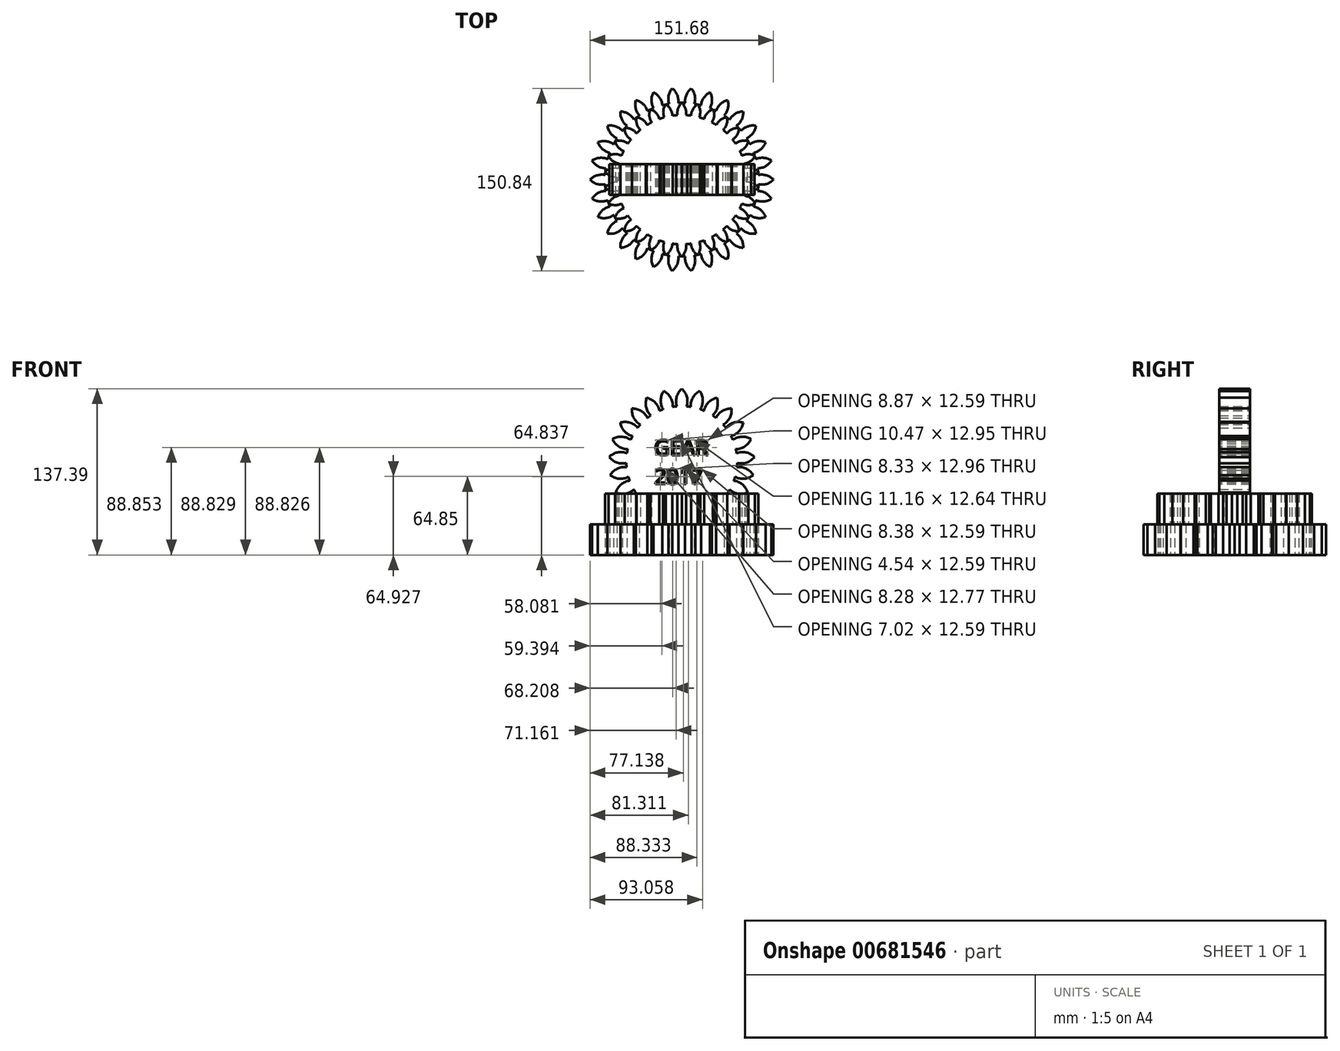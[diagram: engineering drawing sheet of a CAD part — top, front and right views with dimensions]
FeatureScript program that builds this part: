
annotation { "Feature Type Name" : "Feature", "Feature Type Description" : "" }
export const myFeature = defineFeature(function(context is Context, id is Id, definition is map)
    precondition{}
    {
        {
            var Q0;
            Q0=qCreatedBy(makeId("Top.planeOp"),FACE);
            var sketch = newSketch(context, id + "F0", { "sketchPlane" : qUnion([Q0])});
            skCircle(sketch, "E0", {"center": v(0, 0) * mm, "radius": 63.5 * mm});
            skArc(sketch, "E1", {"start": v(-63.38, 3.83) * mm, "mid": v(-70.11, 3.54) * mm, "end": v(-75.84, 0) * mm});
            skArc(sketch, "E2.MirrorCS", {"start": v(-63.38, -3.83) * mm, "mid": v(-70.11, -3.54) * mm, "end": v(-75.84, 0) * mm});
            skArc(sketch, "E3", {"start": v(-63.38, 3.83) * mm, "mid": v(-63.96, 0) * mm, "end": v(-63.38, -3.83) * mm});
            skArc(sketch, "E4.1.0", {"start": v(-62.8, -9.43) * mm, "mid": v(-69.31, -11.11) * mm, "end": v(-74.18, -15.77) * mm});
            skArc(sketch, "E4.1.2", {"start": v(-61.2, -16.92) * mm, "mid": v(-67.84, -18.04) * mm, "end": v(-74.18, -15.77) * mm});
            skArc(sketch, "E4.2.0", {"start": v(-59.46, -22.28) * mm, "mid": v(-65.49, -25.28) * mm, "end": v(-69.28, -30.85) * mm});
            skArc(sketch, "E4.2.2", {"start": v(-56.35, -29.28) * mm, "mid": v(-62.6, -31.75) * mm, "end": v(-69.28, -30.85) * mm});
            skArc(sketch, "E4.3.0", {"start": v(-53.53, -34.16) * mm, "mid": v(-58.8, -38.35) * mm, "end": v(-61.35, -44.58) * mm});
            skArc(sketch, "E4.3.2", {"start": v(-49.03, -40.36) * mm, "mid": v(-54.64, -44.07) * mm, "end": v(-61.35, -44.58) * mm});
            skArc(sketch, "E4.4.0", {"start": v(-45.26, -44.54) * mm, "mid": v(-49.54, -49.73) * mm, "end": v(-50.75, -56.36) * mm});
            skArc(sketch, "E4.4.2", {"start": v(-39.57, -49.67) * mm, "mid": v(-44.28, -54.47) * mm, "end": v(-50.75, -56.36) * mm});
            skArc(sketch, "E4.5.0", {"start": v(-35, -52.98) * mm, "mid": v(-38.12, -58.95) * mm, "end": v(-37.92, -65.68) * mm});
            skArc(sketch, "E4.5.2", {"start": v(-28.38, -56.8) * mm, "mid": v(-31.99, -62.49) * mm, "end": v(-37.92, -65.68) * mm});
            skArc(sketch, "E4.6.0", {"start": v(-23.23, -59.1) * mm, "mid": v(-25.03, -65.59) * mm, "end": v(-23.44, -72.13) * mm});
            skArc(sketch, "E4.6.2", {"start": v(-15.94, -61.47) * mm, "mid": v(-18.3, -67.77) * mm, "end": v(-23.44, -72.13) * mm});
            skArc(sketch, "E4.7.0", {"start": v(-10.43, -62.64) * mm, "mid": v(-10.85, -69.36) * mm, "end": v(-7.93, -75.42) * mm});
            skArc(sketch, "E4.7.2", {"start": v(-2.82, -63.44) * mm, "mid": v(-3.8, -70.1) * mm, "end": v(-7.93, -75.42) * mm});
            skArc(sketch, "E4.8.0", {"start": v(2.82, -63.44) * mm, "mid": v(3.8, -70.1) * mm, "end": v(7.93, -75.42) * mm});
            skArc(sketch, "E4.8.2", {"start": v(10.43, -62.64) * mm, "mid": v(10.85, -69.36) * mm, "end": v(7.93, -75.42) * mm});
            skArc(sketch, "E4.9.0", {"start": v(15.94, -61.47) * mm, "mid": v(18.3, -67.77) * mm, "end": v(23.44, -72.13) * mm});
            skArc(sketch, "E4.9.2", {"start": v(23.23, -59.1) * mm, "mid": v(25.03, -65.59) * mm, "end": v(23.44, -72.13) * mm});
            skArc(sketch, "E4.10.0", {"start": v(28.38, -56.8) * mm, "mid": v(31.99, -62.49) * mm, "end": v(37.92, -65.68) * mm});
            skArc(sketch, "E4.10.2", {"start": v(35, -52.98) * mm, "mid": v(38.12, -58.95) * mm, "end": v(37.92, -65.68) * mm});
            skArc(sketch, "E4.11.0", {"start": v(39.57, -49.67) * mm, "mid": v(44.28, -54.47) * mm, "end": v(50.75, -56.36) * mm});
            skArc(sketch, "E4.11.2", {"start": v(45.26, -44.54) * mm, "mid": v(49.54, -49.73) * mm, "end": v(50.75, -56.36) * mm});
            skArc(sketch, "E4.12.0", {"start": v(49.03, -40.36) * mm, "mid": v(54.64, -44.07) * mm, "end": v(61.35, -44.58) * mm});
            skArc(sketch, "E4.12.2", {"start": v(53.53, -34.16) * mm, "mid": v(58.8, -38.35) * mm, "end": v(61.35, -44.58) * mm});
            skArc(sketch, "E4.13.0", {"start": v(56.35, -29.28) * mm, "mid": v(62.6, -31.75) * mm, "end": v(69.28, -30.85) * mm});
            skArc(sketch, "E4.13.2", {"start": v(59.46, -22.28) * mm, "mid": v(65.49, -25.28) * mm, "end": v(69.28, -30.85) * mm});
            skArc(sketch, "E4.14.0", {"start": v(61.2, -16.92) * mm, "mid": v(67.84, -18.04) * mm, "end": v(74.18, -15.77) * mm});
            skArc(sketch, "E4.14.2", {"start": v(62.8, -9.43) * mm, "mid": v(69.31, -11.11) * mm, "end": v(74.18, -15.77) * mm});
            skArc(sketch, "E5.3.15.0", {"start": v(63.38, -3.83) * mm, "mid": v(70.11, -3.54) * mm, "end": v(75.84, 0) * mm});
            skArc(sketch, "E5.6.15.0", {"start": v(63.38, 3.83) * mm, "mid": v(70.11, 3.54) * mm, "end": v(75.84, 0) * mm});
            skArc(sketch, "E5.3.16.0", {"start": v(62.8, 9.43) * mm, "mid": v(69.31, 11.11) * mm, "end": v(74.18, 15.77) * mm});
            skArc(sketch, "E5.6.16.0", {"start": v(61.2, 16.92) * mm, "mid": v(67.84, 18.04) * mm, "end": v(74.18, 15.77) * mm});
            skArc(sketch, "E5.3.17.0", {"start": v(59.46, 22.28) * mm, "mid": v(65.49, 25.28) * mm, "end": v(69.28, 30.85) * mm});
            skArc(sketch, "E5.6.17.0", {"start": v(56.35, 29.28) * mm, "mid": v(62.6, 31.75) * mm, "end": v(69.28, 30.85) * mm});
            skArc(sketch, "E5.3.18.0", {"start": v(53.53, 34.16) * mm, "mid": v(58.8, 38.35) * mm, "end": v(61.35, 44.58) * mm});
            skArc(sketch, "E5.6.18.0", {"start": v(49.03, 40.36) * mm, "mid": v(54.64, 44.07) * mm, "end": v(61.35, 44.58) * mm});
            skArc(sketch, "E5.3.19.0", {"start": v(45.26, 44.54) * mm, "mid": v(49.54, 49.73) * mm, "end": v(50.75, 56.36) * mm});
            skArc(sketch, "E5.6.19.0", {"start": v(39.57, 49.67) * mm, "mid": v(44.28, 54.47) * mm, "end": v(50.75, 56.36) * mm});
            skArc(sketch, "E5.3.20.0", {"start": v(35, 52.98) * mm, "mid": v(38.12, 58.95) * mm, "end": v(37.92, 65.68) * mm});
            skArc(sketch, "E5.6.20.0", {"start": v(28.38, 56.8) * mm, "mid": v(31.99, 62.49) * mm, "end": v(37.92, 65.68) * mm});
            skArc(sketch, "E5.3.21.0", {"start": v(23.23, 59.1) * mm, "mid": v(25.03, 65.59) * mm, "end": v(23.44, 72.13) * mm});
            skArc(sketch, "E5.6.21.0", {"start": v(15.94, 61.47) * mm, "mid": v(18.3, 67.77) * mm, "end": v(23.44, 72.13) * mm});
            skArc(sketch, "E5.3.22.0", {"start": v(10.43, 62.64) * mm, "mid": v(10.85, 69.36) * mm, "end": v(7.93, 75.42) * mm});
            skArc(sketch, "E5.6.22.0", {"start": v(2.82, 63.44) * mm, "mid": v(3.8, 70.1) * mm, "end": v(7.93, 75.42) * mm});
            skArc(sketch, "E5.3.23.0", {"start": v(-2.82, 63.44) * mm, "mid": v(-3.8, 70.1) * mm, "end": v(-7.93, 75.42) * mm});
            skArc(sketch, "E5.6.23.0", {"start": v(-10.43, 62.64) * mm, "mid": v(-10.85, 69.36) * mm, "end": v(-7.93, 75.42) * mm});
            skArc(sketch, "E5.3.24.0", {"start": v(-15.94, 61.47) * mm, "mid": v(-18.3, 67.77) * mm, "end": v(-23.44, 72.13) * mm});
            skArc(sketch, "E5.6.24.0", {"start": v(-23.23, 59.1) * mm, "mid": v(-25.03, 65.59) * mm, "end": v(-23.44, 72.13) * mm});
            skArc(sketch, "E5.3.25.0", {"start": v(-28.38, 56.8) * mm, "mid": v(-31.99, 62.49) * mm, "end": v(-37.92, 65.68) * mm});
            skArc(sketch, "E5.6.25.0", {"start": v(-35, 52.98) * mm, "mid": v(-38.12, 58.95) * mm, "end": v(-37.92, 65.68) * mm});
            skArc(sketch, "E5.3.26.0", {"start": v(-39.57, 49.67) * mm, "mid": v(-44.28, 54.47) * mm, "end": v(-50.75, 56.36) * mm});
            skArc(sketch, "E5.6.26.0", {"start": v(-45.26, 44.54) * mm, "mid": v(-49.54, 49.73) * mm, "end": v(-50.75, 56.36) * mm});
            skArc(sketch, "E5.3.27.0", {"start": v(-49.03, 40.36) * mm, "mid": v(-54.64, 44.07) * mm, "end": v(-61.35, 44.58) * mm});
            skArc(sketch, "E5.6.27.0", {"start": v(-53.53, 34.16) * mm, "mid": v(-58.8, 38.35) * mm, "end": v(-61.35, 44.58) * mm});
            skArc(sketch, "E5.3.28.0", {"start": v(-56.35, 29.28) * mm, "mid": v(-62.6, 31.75) * mm, "end": v(-69.28, 30.85) * mm});
            skArc(sketch, "E5.6.28.0", {"start": v(-59.46, 22.28) * mm, "mid": v(-65.49, 25.28) * mm, "end": v(-69.28, 30.85) * mm});
            skArc(sketch, "E5.3.29.0", {"start": v(-61.2, 16.92) * mm, "mid": v(-67.84, 18.04) * mm, "end": v(-74.18, 15.77) * mm});
            skArc(sketch, "E5.6.29.0", {"start": v(-62.8, 9.43) * mm, "mid": v(-69.31, 11.11) * mm, "end": v(-74.18, 15.77) * mm});
            skSolve(sketch);
        }
        {
            var Q0;
            Q0 = qSketchRegion(id + "F0", true);
            extrude(context, id + "F1", {"entities" : qUnion([Q0]), "depth" : 25.4 * mm, "offsetDistance" : 25.4 * mm});
        }
        {
            var Q0;
            Q0=makeQuery(id+"F1.opExtrude","CAP_FACE",FACE,{"disambiguationData":[OSD([sQuery(id+"F0.wireOp",EDGE,"E1"),sQuery(id+"F0.wireOp",EDGE,"E2.MirrorCS"),sQuery(id+"F0.wireOp",EDGE,"E4.1.0"),sQuery(id+"F0.wireOp",EDGE,"E4.1.2"),sQuery(id+"F0.wireOp",EDGE,"E4.2.0"),sQuery(id+"F0.wireOp",EDGE,"E4.2.2"),sQuery(id+"F0.wireOp",EDGE,"E4.3.0"),sQuery(id+"F0.wireOp",EDGE,"E4.3.2"),sQuery(id+"F0.wireOp",EDGE,"E4.4.0"),sQuery(id+"F0.wireOp",EDGE,"E4.4.2"),sQuery(id+"F0.wireOp",EDGE,"E4.5.0"),sQuery(id+"F0.wireOp",EDGE,"E4.5.2"),sQuery(id+"F0.wireOp",EDGE,"E4.6.0"),sQuery(id+"F0.wireOp",EDGE,"E4.6.2"),sQuery(id+"F0.wireOp",EDGE,"E4.7.0"),sQuery(id+"F0.wireOp",EDGE,"E4.7.2"),sQuery(id+"F0.wireOp",EDGE,"E4.8.0"),sQuery(id+"F0.wireOp",EDGE,"E4.8.2"),sQuery(id+"F0.wireOp",EDGE,"E4.9.0"),sQuery(id+"F0.wireOp",EDGE,"E4.9.2"),sQuery(id+"F0.wireOp",EDGE,"E4.10.0"),sQuery(id+"F0.wireOp",EDGE,"E4.10.2"),sQuery(id+"F0.wireOp",EDGE,"E4.11.0"),sQuery(id+"F0.wireOp",EDGE,"E4.11.2"),sQuery(id+"F0.wireOp",EDGE,"E4.12.0"),sQuery(id+"F0.wireOp",EDGE,"E4.12.2"),sQuery(id+"F0.wireOp",EDGE,"E4.13.0"),sQuery(id+"F0.wireOp",EDGE,"E4.13.2"),sQuery(id+"F0.wireOp",EDGE,"E4.14.0"),sQuery(id+"F0.wireOp",EDGE,"E4.14.2"),sQuery(id+"F0.wireOp",EDGE,"E5.3.15.0"),sQuery(id+"F0.wireOp",EDGE,"E5.6.15.0"),sQuery(id+"F0.wireOp",EDGE,"E5.3.16.0"),sQuery(id+"F0.wireOp",EDGE,"E5.6.16.0"),sQuery(id+"F0.wireOp",EDGE,"E5.3.17.0"),sQuery(id+"F0.wireOp",EDGE,"E5.6.17.0"),sQuery(id+"F0.wireOp",EDGE,"E5.3.18.0"),sQuery(id+"F0.wireOp",EDGE,"E5.6.18.0"),sQuery(id+"F0.wireOp",EDGE,"E5.3.19.0"),sQuery(id+"F0.wireOp",EDGE,"E5.6.19.0"),sQuery(id+"F0.wireOp",EDGE,"E5.3.20.0"),sQuery(id+"F0.wireOp",EDGE,"E5.6.20.0"),sQuery(id+"F0.wireOp",EDGE,"E5.3.21.0"),sQuery(id+"F0.wireOp",EDGE,"E5.6.21.0"),sQuery(id+"F0.wireOp",EDGE,"E5.3.22.0"),sQuery(id+"F0.wireOp",EDGE,"E5.6.22.0"),sQuery(id+"F0.wireOp",EDGE,"E5.3.23.0"),sQuery(id+"F0.wireOp",EDGE,"E5.6.23.0"),sQuery(id+"F0.wireOp",EDGE,"E5.3.24.0"),sQuery(id+"F0.wireOp",EDGE,"E5.6.24.0"),sQuery(id+"F0.wireOp",EDGE,"E5.3.25.0"),sQuery(id+"F0.wireOp",EDGE,"E5.6.25.0"),sQuery(id+"F0.wireOp",EDGE,"E5.3.26.0"),sQuery(id+"F0.wireOp",EDGE,"E5.6.26.0"),sQuery(id+"F0.wireOp",EDGE,"E5.3.27.0"),sQuery(id+"F0.wireOp",EDGE,"E5.6.27.0"),sQuery(id+"F0.wireOp",EDGE,"E5.3.28.0"),sQuery(id+"F0.wireOp",EDGE,"E5.6.28.0"),sQuery(id+"F0.wireOp",EDGE,"E5.3.29.0"),sQuery(id+"F0.wireOp",EDGE,"E0"),sQuery(id+"F0.wireOp",EDGE,"E5.6.29.0")])],"isStart":false});
            var sketch = newSketch(context, id + "F2", { "sketchPlane" : qUnion([Q0])});
            skCircle(sketch, "E6", {"center": v(0, 0) * mm, "radius": 53.5 * mm});
            skArc(sketch, "E7", {"start": v(-52.74, 9) * mm, "mid": v(-58.36, 9.16) * mm, "end": v(-63.38, 6.64) * mm});
            skPoint(sketch, "E7.endSnap0", {"position": v(-63.15, 6.64) * mm});
            skLineSegment(sketch, "E8", {"start": v(0, 0) * mm, "end": v(-63.15, 6.64) * mm});
            skArc(sketch, "E9.MirrorCS", {"start": v(-53.46, 2.16) * mm, "mid": v(-58.99, 3.17) * mm, "end": v(-63.38, 6.69) * mm});
            skArc(sketch, "E10", {"start": v(-53.46, 2.16) * mm, "mid": v(-53.09, 5.58) * mm, "end": v(-52.74, 9) * mm});
            skArc(sketch, "E11.1.0", {"start": v(-53.46, -2.16) * mm, "mid": v(-58.99, -3.17) * mm, "end": v(-63.38, -6.69) * mm});
            skArc(sketch, "E11.1.1", {"start": v(-52.74, -9) * mm, "mid": v(-58.36, -9.16) * mm, "end": v(-63.38, -6.64) * mm});
            skArc(sketch, "E11.2.0", {"start": v(-51.84, -13.23) * mm, "mid": v(-57.04, -15.37) * mm, "end": v(-60.6, -19.72) * mm});
            skArc(sketch, "E11.2.1", {"start": v(-49.71, -19.77) * mm, "mid": v(-55.18, -21.1) * mm, "end": v(-60.62, -19.67) * mm});
            skArc(sketch, "E11.3.0", {"start": v(-47.96, -23.71) * mm, "mid": v(-52.6, -26.9) * mm, "end": v(-55.18, -31.89) * mm});
            skArc(sketch, "E11.3.1", {"start": v(-44.52, -29.68) * mm, "mid": v(-49.59, -32.1) * mm, "end": v(-55.2, -31.84) * mm});
            skArc(sketch, "E11.4.0", {"start": v(-41.98, -33.17) * mm, "mid": v(-45.86, -37.24) * mm, "end": v(-47.35, -42.66) * mm});
            skArc(sketch, "E11.4.1", {"start": v(-37.37, -38.28) * mm, "mid": v(-41.83, -41.71) * mm, "end": v(-47.38, -42.63) * mm});
            skArc(sketch, "E11.5.0", {"start": v(-34.17, -41.17) * mm, "mid": v(-37.11, -45.96) * mm, "end": v(-37.44, -51.57) * mm});
            skArc(sketch, "E11.5.1", {"start": v(-28.6, -45.22) * mm, "mid": v(-32.24, -49.5) * mm, "end": v(-37.48, -51.55) * mm});
            skArc(sketch, "E11.6.0", {"start": v(-24.86, -47.37) * mm, "mid": v(-26.75, -52.67) * mm, "end": v(-25.9, -58.23) * mm});
            skArc(sketch, "E11.6.1", {"start": v(-18.57, -50.17) * mm, "mid": v(-21.25, -55.12) * mm, "end": v(-25.94, -58.21) * mm});
            skArc(sketch, "E11.7.0", {"start": v(-14.47, -51.5) * mm, "mid": v(-15.21, -57.08) * mm, "end": v(-13.23, -62.34) * mm});
            skArc(sketch, "E11.7.1", {"start": v(-7.73, -52.94) * mm, "mid": v(-9.32, -58.33) * mm, "end": v(-13.27, -62.33) * mm});
            skArc(sketch, "E11.8.0", {"start": v(-3.44, -53.4) * mm, "mid": v(-3.01, -59) * mm, "end": v(0.02, -63.73) * mm});
            skArc(sketch, "E11.8.1", {"start": v(3.44, -53.4) * mm, "mid": v(3.01, -59) * mm, "end": v(-0.02, -63.73) * mm});
            skArc(sketch, "E11.9.0", {"start": v(7.73, -52.94) * mm, "mid": v(9.32, -58.33) * mm, "end": v(13.27, -62.33) * mm});
            skArc(sketch, "E11.9.1", {"start": v(14.47, -51.5) * mm, "mid": v(15.21, -57.08) * mm, "end": v(13.23, -62.34) * mm});
            skArc(sketch, "E11.10.0", {"start": v(18.57, -50.17) * mm, "mid": v(21.25, -55.12) * mm, "end": v(25.94, -58.21) * mm});
            skArc(sketch, "E11.10.1", {"start": v(24.86, -47.37) * mm, "mid": v(26.75, -52.67) * mm, "end": v(25.9, -58.23) * mm});
            skArc(sketch, "E11.11.0", {"start": v(28.6, -45.22) * mm, "mid": v(32.24, -49.5) * mm, "end": v(37.48, -51.55) * mm});
            skArc(sketch, "E11.11.1", {"start": v(34.17, -41.17) * mm, "mid": v(37.11, -45.96) * mm, "end": v(37.44, -51.57) * mm});
            skArc(sketch, "E11.12.0", {"start": v(37.37, -38.28) * mm, "mid": v(41.83, -41.71) * mm, "end": v(47.38, -42.63) * mm});
            skArc(sketch, "E11.12.1", {"start": v(41.98, -33.17) * mm, "mid": v(45.86, -37.24) * mm, "end": v(47.35, -42.66) * mm});
            skArc(sketch, "E11.13.0", {"start": v(44.52, -29.68) * mm, "mid": v(49.59, -32.1) * mm, "end": v(55.2, -31.84) * mm});
            skArc(sketch, "E11.13.1", {"start": v(47.96, -23.71) * mm, "mid": v(52.6, -26.9) * mm, "end": v(55.18, -31.89) * mm});
            skArc(sketch, "E11.14.0", {"start": v(49.71, -19.77) * mm, "mid": v(55.18, -21.1) * mm, "end": v(60.62, -19.67) * mm});
            skArc(sketch, "E11.14.1", {"start": v(51.84, -13.23) * mm, "mid": v(57.04, -15.37) * mm, "end": v(60.6, -19.72) * mm});
            skArc(sketch, "E11.15.0", {"start": v(52.74, -9) * mm, "mid": v(58.36, -9.16) * mm, "end": v(63.38, -6.64) * mm});
            skArc(sketch, "E11.15.1", {"start": v(53.46, -2.16) * mm, "mid": v(58.99, -3.17) * mm, "end": v(63.38, -6.69) * mm});
            skArc(sketch, "E11.16.0", {"start": v(53.46, 2.16) * mm, "mid": v(58.99, 3.17) * mm, "end": v(63.38, 6.69) * mm});
            skArc(sketch, "E11.16.1", {"start": v(52.74, 9) * mm, "mid": v(58.36, 9.16) * mm, "end": v(63.38, 6.64) * mm});
            skArc(sketch, "E11.17.0", {"start": v(51.84, 13.23) * mm, "mid": v(57.04, 15.37) * mm, "end": v(60.6, 19.72) * mm});
            skArc(sketch, "E11.17.1", {"start": v(49.71, 19.77) * mm, "mid": v(55.18, 21.1) * mm, "end": v(60.62, 19.67) * mm});
            skArc(sketch, "E11.18.0", {"start": v(47.96, 23.71) * mm, "mid": v(52.6, 26.9) * mm, "end": v(55.18, 31.89) * mm});
            skArc(sketch, "E11.18.1", {"start": v(44.52, 29.68) * mm, "mid": v(49.59, 32.1) * mm, "end": v(55.2, 31.84) * mm});
            skArc(sketch, "E11.19.0", {"start": v(41.98, 33.17) * mm, "mid": v(45.86, 37.24) * mm, "end": v(47.35, 42.66) * mm});
            skArc(sketch, "E11.19.1", {"start": v(37.37, 38.28) * mm, "mid": v(41.83, 41.71) * mm, "end": v(47.38, 42.63) * mm});
            skArc(sketch, "E11.20.0", {"start": v(34.17, 41.17) * mm, "mid": v(37.11, 45.96) * mm, "end": v(37.44, 51.57) * mm});
            skArc(sketch, "E11.20.1", {"start": v(28.6, 45.22) * mm, "mid": v(32.24, 49.5) * mm, "end": v(37.48, 51.55) * mm});
            skArc(sketch, "E11.21.0", {"start": v(24.86, 47.37) * mm, "mid": v(26.75, 52.67) * mm, "end": v(25.9, 58.23) * mm});
            skArc(sketch, "E11.21.1", {"start": v(18.57, 50.17) * mm, "mid": v(21.25, 55.12) * mm, "end": v(25.94, 58.21) * mm});
            skArc(sketch, "E11.22.0", {"start": v(14.47, 51.5) * mm, "mid": v(15.21, 57.08) * mm, "end": v(13.23, 62.34) * mm});
            skArc(sketch, "E11.22.1", {"start": v(7.73, 52.94) * mm, "mid": v(9.32, 58.33) * mm, "end": v(13.27, 62.33) * mm});
            skArc(sketch, "E11.23.0", {"start": v(3.44, 53.4) * mm, "mid": v(3.01, 59) * mm, "end": v(-0.02, 63.73) * mm});
            skArc(sketch, "E11.23.1", {"start": v(-3.44, 53.4) * mm, "mid": v(-3.01, 59) * mm, "end": v(0.02, 63.73) * mm});
            skArc(sketch, "E11.24.0", {"start": v(-7.73, 52.94) * mm, "mid": v(-9.32, 58.33) * mm, "end": v(-13.27, 62.33) * mm});
            skArc(sketch, "E11.24.1", {"start": v(-14.47, 51.5) * mm, "mid": v(-15.21, 57.08) * mm, "end": v(-13.23, 62.34) * mm});
            skArc(sketch, "E11.25.0", {"start": v(-18.57, 50.17) * mm, "mid": v(-21.25, 55.12) * mm, "end": v(-25.94, 58.21) * mm});
            skArc(sketch, "E11.25.1", {"start": v(-24.86, 47.37) * mm, "mid": v(-26.75, 52.67) * mm, "end": v(-25.9, 58.23) * mm});
            skArc(sketch, "E11.26.0", {"start": v(-28.6, 45.22) * mm, "mid": v(-32.24, 49.5) * mm, "end": v(-37.48, 51.55) * mm});
            skArc(sketch, "E11.26.1", {"start": v(-34.17, 41.17) * mm, "mid": v(-37.11, 45.96) * mm, "end": v(-37.44, 51.57) * mm});
            skArc(sketch, "E11.27.0", {"start": v(-37.37, 38.28) * mm, "mid": v(-41.83, 41.71) * mm, "end": v(-47.38, 42.63) * mm});
            skArc(sketch, "E11.27.1", {"start": v(-41.98, 33.17) * mm, "mid": v(-45.86, 37.24) * mm, "end": v(-47.35, 42.66) * mm});
            skArc(sketch, "E11.28.0", {"start": v(-44.52, 29.68) * mm, "mid": v(-49.59, 32.1) * mm, "end": v(-55.2, 31.84) * mm});
            skArc(sketch, "E11.28.1", {"start": v(-47.96, 23.71) * mm, "mid": v(-52.6, 26.9) * mm, "end": v(-55.18, 31.89) * mm});
            skArc(sketch, "E11.29.0", {"start": v(-49.71, 19.77) * mm, "mid": v(-55.18, 21.1) * mm, "end": v(-60.62, 19.67) * mm});
            skArc(sketch, "E11.29.1", {"start": v(-51.84, 13.23) * mm, "mid": v(-57.04, 15.37) * mm, "end": v(-60.6, 19.72) * mm});
            skSolve(sketch);
        }
        {
            var Q0;
            Q0 = qSketchRegion(id + "F2", true);
            extrude(context, id + "F3", {"entities" : qUnion([Q0]), "operationType" : NewBodyOperationType.ADD, "depth" : 25.4 * mm, "offsetDistance" : 25.4 * mm});
        }
        {
            var Q0;
            Q0=qCreatedBy(makeId("Front.planeOp"),FACE);
            var sketch = newSketch(context, id + "F4", { "sketchPlane" : qUnion([Q0])});
            skCircle(sketch, "E12", {"center": v(0, 77.24) * mm, "radius": 45.85 * mm});
            skArc(sketch, "E13", {"start": v(4.07, 122.9) * mm, "mid": v(4.18, 130.75) * mm, "end": v(0, 137.39) * mm});
            skArc(sketch, "E14.MirrorCS", {"start": v(-4.07, 122.9) * mm, "mid": v(-4.18, 130.75) * mm, "end": v(0, 137.39) * mm});
            skArc(sketch, "E15", {"start": v(-4.07, 122.9) * mm, "mid": v(0, 122.88) * mm, "end": v(4.07, 122.9) * mm});
            skPoint(sketch, "E16.center", {"position": v(0, 0) * mm});
            skArc(sketch, "E17.1.0", {"start": v(-15.3, 120.46) * mm, "mid": v(-17.36, 128.03) * mm, "end": v(-14.96, 135.5) * mm});
            skArc(sketch, "E17.1.1", {"start": v(-7.42, 122.48) * mm, "mid": v(-9.26, 130.1) * mm, "end": v(-14.96, 135.5) * mm});
            skArc(sketch, "E17.2.0", {"start": v(-25.56, 115.3) * mm, "mid": v(-29.44, 122.11) * mm, "end": v(-28.98, 129.95) * mm});
            skArc(sketch, "E17.2.1", {"start": v(-18.44, 119.21) * mm, "mid": v(-22.12, 126.14) * mm, "end": v(-28.98, 129.95) * mm});
            skArc(sketch, "E17.3.0", {"start": v(-34.23, 107.74) * mm, "mid": v(-39.68, 113.38) * mm, "end": v(-41.18, 121.08) * mm});
            skArc(sketch, "E17.3.1", {"start": v(-28.3, 113.3) * mm, "mid": v(-33.58, 119.1) * mm, "end": v(-41.18, 121.08) * mm});
            skArc(sketch, "E17.4.0", {"start": v(-40.74, 98.27) * mm, "mid": v(-47.42, 102.38) * mm, "end": v(-50.79, 109.47) * mm});
            skArc(sketch, "E17.4.1", {"start": v(-36.38, 105.14) * mm, "mid": v(-42.94, 109.44) * mm, "end": v(-50.79, 109.47) * mm});
            skArc(sketch, "E17.5.0", {"start": v(-44.69, 87.48) * mm, "mid": v(-52.18, 89.8) * mm, "end": v(-57.2, 95.82) * mm});
            skArc(sketch, "E17.5.1", {"start": v(-42.17, 95.22) * mm, "mid": v(-49.6, 97.75) * mm, "end": v(-57.2, 95.82) * mm});
            skArc(sketch, "E17.6.0", {"start": v(-45.83, 76.04) * mm, "mid": v(-53.67, 76.42) * mm, "end": v(-60.03, 81.01) * mm});
            skArc(sketch, "E17.6.1", {"start": v(-45.32, 84.16) * mm, "mid": v(-53.14, 84.77) * mm, "end": v(-60.03, 81.01) * mm});
            skArc(sketch, "E17.7.0", {"start": v(-44.1, 64.68) * mm, "mid": v(-51.78, 63.1) * mm, "end": v(-59.08, 65.97) * mm});
            skArc(sketch, "E17.7.1", {"start": v(-45.62, 72.67) * mm, "mid": v(-53.35, 71.32) * mm, "end": v(-59.08, 65.97) * mm});
            skArc(sketch, "E17.8.0", {"start": v(-39.59, 54.11) * mm, "mid": v(-46.64, 50.67) * mm, "end": v(-54.42, 51.63) * mm});
            skArc(sketch, "E17.8.1", {"start": v(-43.05, 61.47) * mm, "mid": v(-50.2, 58.23) * mm, "end": v(-54.42, 51.63) * mm});
            skArc(sketch, "E17.9.0", {"start": v(-32.6, 45) * mm, "mid": v(-38.57, 39.9) * mm, "end": v(-46.35, 38.9) * mm});
            skArc(sketch, "E17.9.1", {"start": v(-37.78, 51.26) * mm, "mid": v(-43.9, 46.35) * mm, "end": v(-46.35, 38.9) * mm});
            skArc(sketch, "E17.10.0", {"start": v(-23.55, 37.9) * mm, "mid": v(-28.07, 31.49) * mm, "end": v(-35.35, 28.57) * mm});
            skArc(sketch, "E17.10.1", {"start": v(-30.13, 42.68) * mm, "mid": v(-34.84, 36.4) * mm, "end": v(-35.35, 28.57) * mm});
            skArc(sketch, "E17.11.0", {"start": v(-13.03, 33.28) * mm, "mid": v(-15.81, 25.94) * mm, "end": v(-22.14, 21.31) * mm});
            skArc(sketch, "E17.11.1", {"start": v(-20.6, 36.27) * mm, "mid": v(-23.59, 29.02) * mm, "end": v(-22.14, 21.31) * mm});
            skArc(sketch, "E17.12.0", {"start": v(-1.69, 31.42) * mm, "mid": v(-2.56, 23.62) * mm, "end": v(-7.54, 17.56) * mm});
            skArc(sketch, "E17.12.1", {"start": v(-9.76, 32.44) * mm, "mid": v(-10.85, 24.67) * mm, "end": v(-7.54, 17.56) * mm});
            skArc(sketch, "E17.13.0", {"start": v(9.76, 32.44) * mm, "mid": v(10.85, 24.67) * mm, "end": v(7.54, 17.56) * mm});
            skArc(sketch, "E17.13.1", {"start": v(1.69, 31.42) * mm, "mid": v(2.56, 23.62) * mm, "end": v(7.54, 17.56) * mm});
            skArc(sketch, "E17.14.0", {"start": v(20.6, 36.27) * mm, "mid": v(23.59, 29.02) * mm, "end": v(22.14, 21.31) * mm});
            skArc(sketch, "E17.14.1", {"start": v(13.03, 33.28) * mm, "mid": v(15.81, 25.94) * mm, "end": v(22.14, 21.31) * mm});
            skArc(sketch, "E17.15.0", {"start": v(30.13, 42.68) * mm, "mid": v(34.84, 36.4) * mm, "end": v(35.35, 28.57) * mm});
            skArc(sketch, "E17.15.1", {"start": v(23.55, 37.9) * mm, "mid": v(28.07, 31.49) * mm, "end": v(35.35, 28.57) * mm});
            skArc(sketch, "E17.16.0", {"start": v(37.78, 51.26) * mm, "mid": v(43.9, 46.35) * mm, "end": v(46.35, 38.9) * mm});
            skArc(sketch, "E17.16.1", {"start": v(32.6, 45) * mm, "mid": v(38.57, 39.9) * mm, "end": v(46.35, 38.9) * mm});
            skArc(sketch, "E17.17.0", {"start": v(43.05, 61.47) * mm, "mid": v(50.2, 58.23) * mm, "end": v(54.42, 51.63) * mm});
            skArc(sketch, "E17.17.1", {"start": v(39.59, 54.11) * mm, "mid": v(46.64, 50.67) * mm, "end": v(54.42, 51.63) * mm});
            skArc(sketch, "E17.18.0", {"start": v(45.62, 72.67) * mm, "mid": v(53.35, 71.32) * mm, "end": v(59.08, 65.97) * mm});
            skArc(sketch, "E17.18.1", {"start": v(44.1, 64.68) * mm, "mid": v(51.78, 63.1) * mm, "end": v(59.08, 65.97) * mm});
            skArc(sketch, "E17.19.0", {"start": v(45.32, 84.16) * mm, "mid": v(53.14, 84.77) * mm, "end": v(60.03, 81.01) * mm});
            skArc(sketch, "E17.19.1", {"start": v(45.83, 76.04) * mm, "mid": v(53.67, 76.42) * mm, "end": v(60.03, 81.01) * mm});
            skArc(sketch, "E17.20.0", {"start": v(42.17, 95.22) * mm, "mid": v(49.6, 97.75) * mm, "end": v(57.2, 95.82) * mm});
            skArc(sketch, "E17.20.1", {"start": v(44.69, 87.48) * mm, "mid": v(52.18, 89.8) * mm, "end": v(57.2, 95.82) * mm});
            skArc(sketch, "E17.21.0", {"start": v(36.38, 105.14) * mm, "mid": v(42.94, 109.44) * mm, "end": v(50.79, 109.47) * mm});
            skArc(sketch, "E17.21.1", {"start": v(40.74, 98.27) * mm, "mid": v(47.42, 102.38) * mm, "end": v(50.79, 109.47) * mm});
            skArc(sketch, "E17.22.0", {"start": v(28.3, 113.3) * mm, "mid": v(33.58, 119.1) * mm, "end": v(41.18, 121.08) * mm});
            skArc(sketch, "E17.22.1", {"start": v(34.23, 107.74) * mm, "mid": v(39.68, 113.38) * mm, "end": v(41.18, 121.08) * mm});
            skArc(sketch, "E17.23.0", {"start": v(18.44, 119.21) * mm, "mid": v(22.12, 126.14) * mm, "end": v(28.98, 129.95) * mm});
            skArc(sketch, "E17.23.1", {"start": v(25.56, 115.3) * mm, "mid": v(29.44, 122.11) * mm, "end": v(28.98, 129.95) * mm});
            skArc(sketch, "E17.24.0", {"start": v(7.42, 122.48) * mm, "mid": v(9.26, 130.1) * mm, "end": v(14.96, 135.5) * mm});
            skArc(sketch, "E17.24.1", {"start": v(15.3, 120.46) * mm, "mid": v(17.36, 128.03) * mm, "end": v(14.96, 135.5) * mm});
            skSolve(sketch);
        }
        {
            var Q0;
            Q0 = qSketchRegion(id + "F4", true);
            extrude(context, id + "F5", {"entities" : qUnion([Q0]), "operationType" : NewBodyOperationType.ADD, "endBound" : BoundingType.SYMMETRIC, "depth" : 25.4 * mm, "offsetDistance" : 25.4 * mm});
        }
        {
            var Q0;
            Q0=makeQuery(id+"F5.opExtrude","CAP_FACE",FACE,{"disambiguationData":[OSD([sQuery(id+"F4.wireOp",EDGE,"E12"),sQuery(id+"F4.wireOp",EDGE,"E13"),sQuery(id+"F4.wireOp",EDGE,"E14.MirrorCS"),sQuery(id+"F4.wireOp",EDGE,"E17.1.0"),sQuery(id+"F4.wireOp",EDGE,"E17.1.1"),sQuery(id+"F4.wireOp",EDGE,"E17.2.0"),sQuery(id+"F4.wireOp",EDGE,"E17.2.1"),sQuery(id+"F4.wireOp",EDGE,"E17.3.0"),sQuery(id+"F4.wireOp",EDGE,"E17.3.1"),sQuery(id+"F4.wireOp",EDGE,"E17.4.0"),sQuery(id+"F4.wireOp",EDGE,"E17.4.1"),sQuery(id+"F4.wireOp",EDGE,"E17.5.0"),sQuery(id+"F4.wireOp",EDGE,"E17.5.1"),sQuery(id+"F4.wireOp",EDGE,"E17.6.0"),sQuery(id+"F4.wireOp",EDGE,"E17.6.1"),sQuery(id+"F4.wireOp",EDGE,"E17.7.0"),sQuery(id+"F4.wireOp",EDGE,"E17.7.1"),sQuery(id+"F4.wireOp",EDGE,"E17.8.0"),sQuery(id+"F4.wireOp",EDGE,"E17.8.1"),sQuery(id+"F4.wireOp",EDGE,"E17.9.0"),sQuery(id+"F4.wireOp",EDGE,"E17.9.1"),sQuery(id+"F4.wireOp",EDGE,"E17.10.0"),sQuery(id+"F4.wireOp",EDGE,"E17.10.1"),sQuery(id+"F4.wireOp",EDGE,"E17.11.0"),sQuery(id+"F4.wireOp",EDGE,"E17.11.1"),sQuery(id+"F4.wireOp",EDGE,"E17.12.0"),sQuery(id+"F4.wireOp",EDGE,"E17.12.1"),sQuery(id+"F4.wireOp",EDGE,"E17.13.0"),sQuery(id+"F4.wireOp",EDGE,"E17.13.1"),sQuery(id+"F4.wireOp",EDGE,"E17.14.0"),sQuery(id+"F4.wireOp",EDGE,"E17.14.1"),sQuery(id+"F4.wireOp",EDGE,"E17.15.0"),sQuery(id+"F4.wireOp",EDGE,"E17.15.1"),sQuery(id+"F4.wireOp",EDGE,"E17.16.0"),sQuery(id+"F4.wireOp",EDGE,"E17.16.1"),sQuery(id+"F4.wireOp",EDGE,"E17.17.0"),sQuery(id+"F4.wireOp",EDGE,"E17.17.1"),sQuery(id+"F4.wireOp",EDGE,"E17.18.0"),sQuery(id+"F4.wireOp",EDGE,"E17.18.1"),sQuery(id+"F4.wireOp",EDGE,"E17.19.0"),sQuery(id+"F4.wireOp",EDGE,"E17.19.1"),sQuery(id+"F4.wireOp",EDGE,"E17.20.0"),sQuery(id+"F4.wireOp",EDGE,"E17.20.1"),sQuery(id+"F4.wireOp",EDGE,"E17.21.0"),sQuery(id+"F4.wireOp",EDGE,"E17.21.1"),sQuery(id+"F4.wireOp",EDGE,"E17.22.0"),sQuery(id+"F4.wireOp",EDGE,"E17.22.1"),sQuery(id+"F4.wireOp",EDGE,"E17.23.0"),sQuery(id+"F4.wireOp",EDGE,"E17.23.1"),sQuery(id+"F4.wireOp",EDGE,"E17.24.0"),sQuery(id+"F4.wireOp",EDGE,"E17.24.1")])],"isStart":false});
            var sketch = newSketch(context, id + "F6", { "sketchPlane" : qUnion([Q0])});
            skText(sketch, "E18", { "text": "GEAR\n2017", "fontName": "OpenSans-Regular.ttf"});
            const initialGuessF6  = {"E18": [-0.02276, 0.08253, 1, 0, 0.0127]};
            skSetInitialGuess(sketch, initialGuessF6);
            skSolve(sketch);
        }
        {
            var Q0;
            Q0 = qSketchRegion(id + "F6", true);
            extrude(context, id + "F7", {"entities" : qUnion([Q0]), "operationType" : NewBodyOperationType.REMOVE, "endBound" : BoundingType.THROUGH_ALL, "oppositeDirection" : true, "depth" : 2.54 * mm, "offsetDistance" : 25.4 * mm});
        }
    });
